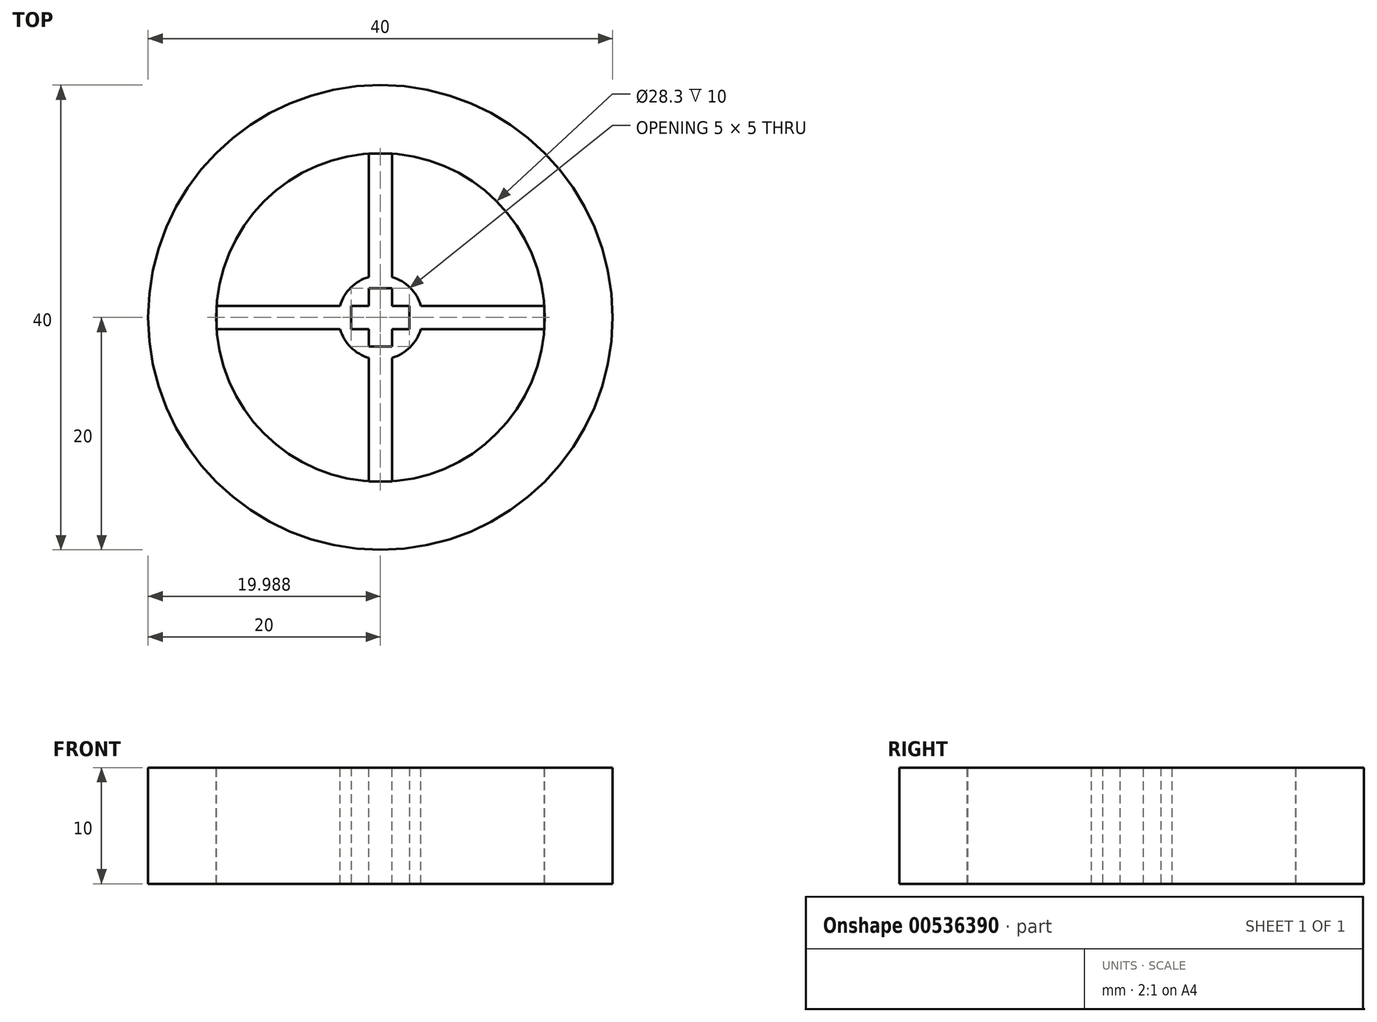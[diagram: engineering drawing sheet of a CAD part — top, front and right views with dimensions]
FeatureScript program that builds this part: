
annotation { "Feature Type Name" : "Feature", "Feature Type Description" : "" }
export const myFeature = defineFeature(function(context is Context, id is Id, definition is map)
    precondition{}
    {
        {
            var Q0;
            Q0=qCreatedBy(makeId("Top.planeOp"),FACE);
            var sketch = newSketch(context, id + "F0", { "sketchPlane" : qUnion([Q0])});
            skLineSegment(sketch, "E0.bottom", {"start": v(-2.51, 1) * mm, "end": v(2.49, 1) * mm});
            skLineSegment(sketch, "E0.top", {"start": v(-2.51, -1) * mm, "end": v(2.49, -1) * mm});
            skLineSegment(sketch, "E0.left", {"start": v(-2.51, 1) * mm, "end": v(-2.51, -1) * mm});
            skLineSegment(sketch, "E0.right", {"start": v(2.49, 1) * mm, "end": v(2.49, -1) * mm});
            skLineSegment(sketch, "E1.bottom", {"start": v(-0.99, 2.5) * mm, "end": v(1.01, 2.5) * mm});
            skLineSegment(sketch, "E1.top", {"start": v(-0.99, -2.5) * mm, "end": v(1.01, -2.5) * mm});
            skLineSegment(sketch, "E1.left", {"start": v(-0.99, 2.5) * mm, "end": v(-0.99, -2.5) * mm});
            skLineSegment(sketch, "E1.right", {"start": v(1.01, 2.5) * mm, "end": v(1.01, -2.5) * mm});
            skSolve(sketch);
        }
        {
            var Q0;
            Q0=qCreatedBy(makeId("Top.planeOp"),FACE);
            var sketch = newSketch(context, id + "F1", { "sketchPlane" : qUnion([Q0])});
            skCircle(sketch, "E2", {"center": v(0, 0) * mm, "radius": 3.62 * mm});
            skSolve(sketch);
        }
        {
            var Q0;
            Q0=makeQuery(id+"F1.imprint","IMPRINT",FACE,{"disambiguationData":[TD([[makeQuery(id+"F1.imprint","IMPRINT",EDGE,{"derivedFrom":sQuery(id+"F1.wireOp",EDGE,"E2")}),1.0]])]});
            extrude(context, id + "F2", {"entities" : qUnion([Q0]), "depth" : 10 * mm, "offsetDistance" : 25 * mm});
        }
        {
            var Q0;
            {var subQ0=sQuery(id+"F0.wireOp",EDGE,"E1.left");var subQ1=sQuery(id+"F0.wireOp",EDGE,"E0.bottom");var subQ2=makeQuery(id+"F0.imprint","INTERSECT",VERTEX,{"derivedFrom":[subQ1,subQ0]});Q0=makeQuery(id+"F0.imprint","IMPRINT",FACE,{"disambiguationData":[TD([[makeQuery(id+"F0.imprint","IMPRINT",EDGE,{"disambiguationData":[TD([[subQ2,-1.0]])],"derivedFrom":subQ1}),-1.0]])]});}
            var Q1;
            {var subQ0=sQuery(id+"F0.wireOp",EDGE,"E0.right");Q1=makeQuery(id+"F0.imprint","IMPRINT",FACE,{"disambiguationData":[TD([[makeQuery(id+"F0.imprint","IMPRINT",EDGE,{"derivedFrom":subQ0}),-1.0]])]});}
            var Q2;
            {var subQ5=sQuery(id+"F0.wireOp",EDGE,"E1.top");Q2=makeQuery(id+"F0.imprint","IMPRINT",FACE,{"disambiguationData":[TD([[makeQuery(id+"F0.imprint","IMPRINT",EDGE,{"derivedFrom":subQ5}),1.0]])]});}
            var Q3;
            {var subQ5=sQuery(id+"F0.wireOp",EDGE,"E1.bottom");Q3=makeQuery(id+"F0.imprint","IMPRINT",FACE,{"disambiguationData":[TD([[makeQuery(id+"F0.imprint","IMPRINT",EDGE,{"derivedFrom":subQ5}),-1.0]])]});}
            var Q4;
            {var subQ0=sQuery(id+"F0.wireOp",EDGE,"E0.left");Q4=makeQuery(id+"F0.imprint","IMPRINT",FACE,{"disambiguationData":[TD([[makeQuery(id+"F0.imprint","IMPRINT",EDGE,{"derivedFrom":subQ0}),1.0]])]});}
            var Q5;
            Q5 = qSketchRegion(id + "F3iHN0mLzB50SuE_2", true);
            extrude(context, id + "F3", {"entities" : qUnion([Q0, Q1, Q2, Q3, Q4, Q5]), "operationType" : NewBodyOperationType.REMOVE, "depth" : 10 * mm, "offsetDistance" : 25 * mm});
        }
        {
            var Q0;
            Q0=makeQuery(id+"F2.opExtrude","CAP_FACE",FACE,{"disambiguationData":[OSD([sQuery(id+"F1.wireOp",EDGE,"E2")])],"isStart":false});
            var sketch = newSketch(context, id + "F4", { "sketchPlane" : qUnion([Q0])});
            skCircle(sketch, "E3", {"center": v(0, 0) * mm, "radius": 20 * mm});
            skCircle(sketch, "E4", {"center": v(0, 0) * mm, "radius": 14.15 * mm});
            skLineSegment(sketch, "E5", {"start": v(-0.99, -2.5) * mm, "end": v(-0.99, -14.11) * mm});
            skLineSegment(sketch, "E6", {"start": v(1.01, -2.5) * mm, "end": v(1.01, -14.11) * mm});
            skLineSegment(sketch, "E7", {"start": v(1.01, -14.11) * mm, "end": v(-0.99, -14.11) * mm});
            skLineSegment(sketch, "E8", {"start": v(2.49, 1) * mm, "end": v(14.11, 1) * mm});
            skLineSegment(sketch, "E9", {"start": v(2.49, -1) * mm, "end": v(14.11, -1) * mm});
            skLineSegment(sketch, "E10", {"start": v(14.11, -1) * mm, "end": v(14.11, 1) * mm});
            skLineSegment(sketch, "E11", {"start": v(1.01, 2.5) * mm, "end": v(1.01, 14.11) * mm});
            skLineSegment(sketch, "E12", {"start": v(-0.99, 2.5) * mm, "end": v(-0.99, 14.11) * mm});
            skLineSegment(sketch, "E13", {"start": v(-0.99, 14.11) * mm, "end": v(1.01, 14.11) * mm});
            skLineSegment(sketch, "E14", {"start": v(-2.51, 1) * mm, "end": v(-14.11, 1) * mm});
            skLineSegment(sketch, "E15", {"start": v(-2.51, -1) * mm, "end": v(-14.11, -1) * mm});
            skLineSegment(sketch, "E16", {"start": v(-14.11, -1) * mm, "end": v(-14.11, 1) * mm});
            skSolve(sketch);
        }
        {
            var Q0;
            {var subQ0=sQuery(id+"F4.wireOp",EDGE,"E13");Q0=makeQuery(id+"F4.imprint","IMPRINT",FACE,{"disambiguationData":[TD([[makeQuery(id+"F4.imprint","IMPRINT",EDGE,{"derivedFrom":subQ0}),-1.0]])]});}
            var Q1;
            {var subQ0=sQuery(id+"F4.wireOp",EDGE,"E10");Q1=makeQuery(id+"F4.imprint","IMPRINT",FACE,{"disambiguationData":[TD([[makeQuery(id+"F4.imprint","IMPRINT",EDGE,{"derivedFrom":subQ0}),1.0]])]});}
            var Q2;
            {var subQ0=sQuery(id+"F4.wireOp",EDGE,"E7");Q2=makeQuery(id+"F4.imprint","IMPRINT",FACE,{"disambiguationData":[TD([[makeQuery(id+"F4.imprint","IMPRINT",EDGE,{"derivedFrom":subQ0}),-1.0]])]});}
            var Q3;
            {var subQ0=sQuery(id+"F4.wireOp",EDGE,"E16");Q3=makeQuery(id+"F4.imprint","IMPRINT",FACE,{"disambiguationData":[TD([[makeQuery(id+"F4.imprint","IMPRINT",EDGE,{"derivedFrom":subQ0}),-1.0]])]});}
            var Q4;
            Q4=makeQuery(id+"F4.imprint","IMPRINT",FACE,{"disambiguationData":[TD([[makeQuery(id+"F4.imprint","IMPRINT",EDGE,{"derivedFrom":sQuery(id+"F4.wireOp",EDGE,"E3")}),1.0]])]});
            extrude(context, id + "F5", {"entities" : qUnion([Q0, Q1, Q2, Q3, Q4]), "operationType" : NewBodyOperationType.ADD, "oppositeDirection" : true, "depth" : 10 * mm, "offsetDistance" : 25 * mm});
        }
    });
